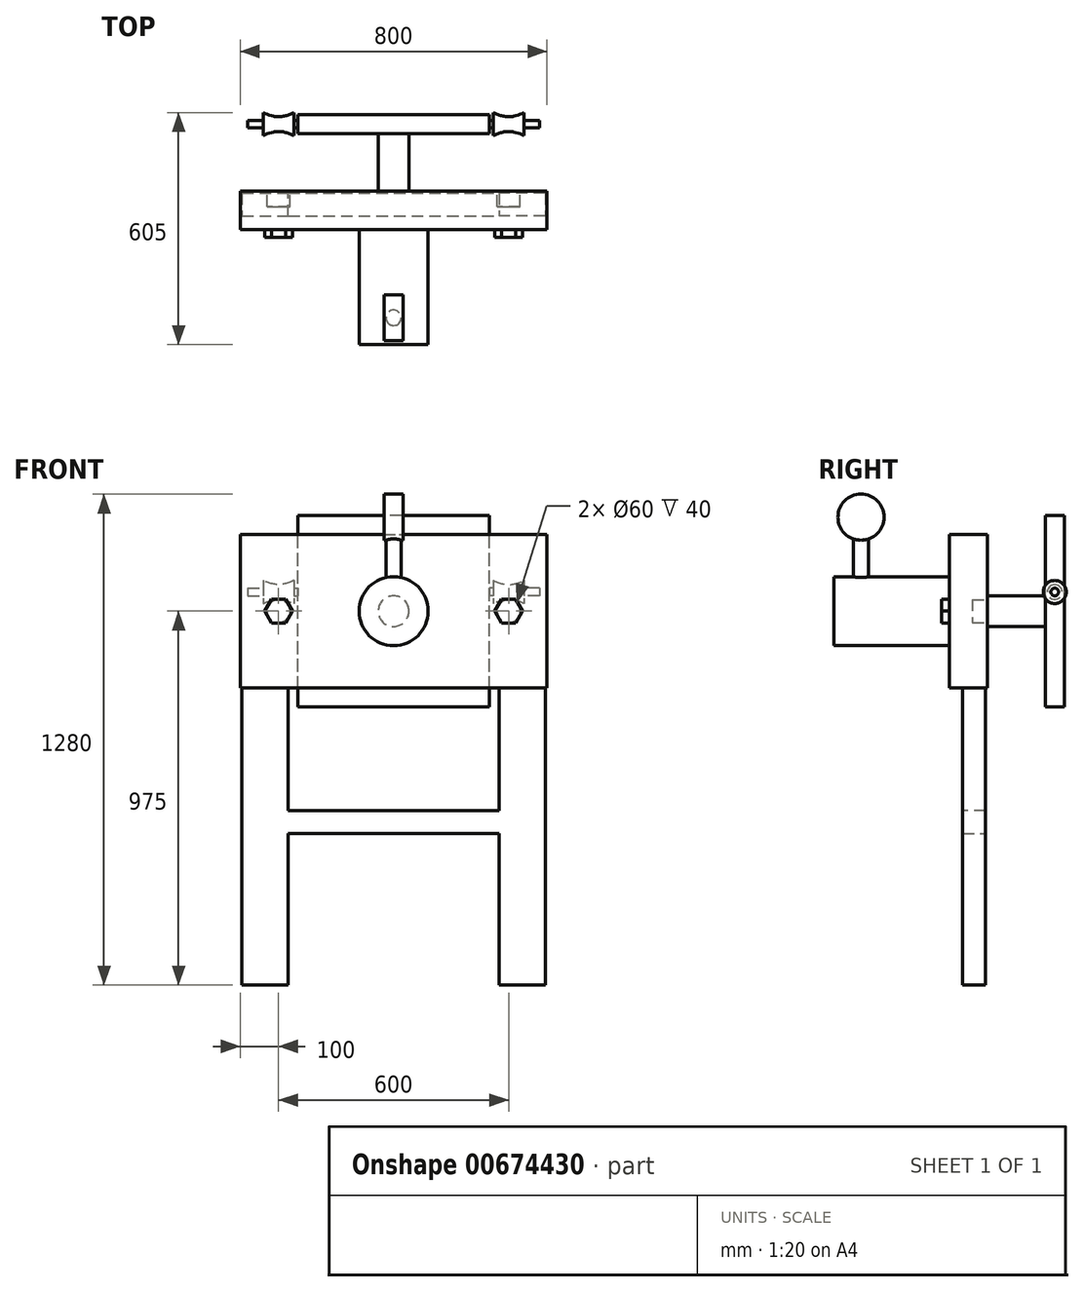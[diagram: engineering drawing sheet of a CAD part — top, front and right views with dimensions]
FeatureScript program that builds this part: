
annotation { "Feature Type Name" : "Feature", "Feature Type Description" : "" }
export const myFeature = defineFeature(function(context is Context, id is Id, definition is map)
    precondition{}
    {
        {
            var Q0;
            Q0=qCreatedBy(makeId("Front.planeOp"),FACE);
            var sketch = newSketch(context, id + "F0", { "sketchPlane" : qUnion([Q0])});
            skLineSegment(sketch, "E0.bottom", {"start": v(-400, -200) * mm, "end": v(400, -200) * mm});
            skLineSegment(sketch, "E0.top", {"start": v(-400, 200) * mm, "end": v(400, 200) * mm});
            skLineSegment(sketch, "E0.left", {"start": v(-400, -200) * mm, "end": v(-400, 200) * mm});
            skLineSegment(sketch, "E0.right", {"start": v(400, -200) * mm, "end": v(400, 200) * mm});
            skPoint(sketch, "E0.middle", {"position": v(0, 0) * mm});
            skSolve(sketch);
        }
        {
            var Q0;
            Q0=makeQuery(id+"F0.imprint","IMPRINT",FACE,{"disambiguationData":[TD([[makeQuery(id+"F0.imprint","IMPRINT",EDGE,{"derivedFrom":sQuery(id+"F0.wireOp",EDGE,"E0.bottom")}),1.0]])]});
            extrude(context, id + "F1", {"entities" : qUnion([Q0]), "endBound" : BoundingType.SYMMETRIC, "depth" : 100 * mm, "offsetDistance" : 25 * mm});
        }
        {
            var Q0;
            Q0=makeQuery(id+"F1.opExtrude","CAP_FACE",FACE,{"disambiguationData":[OSD([sQuery(id+"F0.wireOp",EDGE,"E0.bottom"),sQuery(id+"F0.wireOp",EDGE,"E0.top"),sQuery(id+"F0.wireOp",EDGE,"E0.left"),sQuery(id+"F0.wireOp",EDGE,"E0.right")])],"isStart":false});
            var sketch = newSketch(context, id + "F2", { "sketchPlane" : qUnion([Q0])});
            skCircle(sketch, "E1", {"center": v(0, 0) * mm, "radius": 90 * mm});
            skSolve(sketch);
        }
        {
            var Q0;
            Q0=makeQuery(id+"F2.imprint","IMPRINT",FACE,{"disambiguationData":[TD([[makeQuery(id+"F2.imprint","IMPRINT",EDGE,{"derivedFrom":sQuery(id+"F2.wireOp",EDGE,"E1")}),1.0]])]});
            var Q1;
            Q1=sQuery(id+"F2.wireOp",EDGE,"E1");
            extrude(context, id + "F3", {"entities" : qUnion([Q0]), "operationType" : NewBodyOperationType.ADD, "surfaceEntities" : qUnion([Q1]), "depth" : 300 * mm, "offsetDistance" : 25 * mm});
        }
        {
            var Q0;
            Q0=qCreatedBy(makeId("Top.planeOp"),FACE);
            var sketch = newSketch(context, id + "F4", { "sketchPlane" : qUnion([Q0])});
            skCircle(sketch, "E2", {"center": v(0, -280) * mm, "radius": 20 * mm});
            skSolve(sketch);
        }
        {
            var Q0;
            Q0 = qSketchRegion(id + "F4", true);
            extrude(context, id + "F5", {"entities" : qUnion([Q0]), "operationType" : NewBodyOperationType.ADD, "depth" : 200 * mm, "offsetDistance" : 25 * mm});
        }
        {
            var Q0;
            Q0=qCreatedBy(makeId("Right.planeOp"),FACE);
            var sketch = newSketch(context, id + "F6", { "sketchPlane" : qUnion([Q0])});
            skCircle(sketch, "E3", {"center": v(-280, 245) * mm, "radius": 60 * mm});
            skSolve(sketch);
        }
        {
            var Q0;
            Q0=makeQuery(id+"F6.imprint","IMPRINT",FACE,{"disambiguationData":[TD([[makeQuery(id+"F6.imprint","IMPRINT",EDGE,{"derivedFrom":sQuery(id+"F6.wireOp",EDGE,"E3")}),1.0]])]});
            extrude(context, id + "F7", {"entities" : qUnion([Q0]), "operationType" : NewBodyOperationType.ADD, "endBound" : BoundingType.SYMMETRIC, "depth" : 50 * mm, "offsetDistance" : 25 * mm});
        }
        {
            var Q0;
            Q0=makeQuery(id+"F1.opExtrude","CAP_FACE",FACE,{"disambiguationData":[OSD([sQuery(id+"F0.wireOp",EDGE,"E0.bottom"),sQuery(id+"F0.wireOp",EDGE,"E0.top"),sQuery(id+"F0.wireOp",EDGE,"E0.left"),sQuery(id+"F0.wireOp",EDGE,"E0.right")])],"isStart":false});
            var sketch = newSketch(context, id + "F8", { "sketchPlane" : qUnion([Q0])});
            skCircle(sketch, "E4.cCircle", {"center": v(-300, 0) * mm, "radius": 31.63 * mm, "construction": true});
            skLineSegment(sketch, "E4.0", {"start": v(-281.74, -31.63) * mm, "end": v(-318.26, -31.63) * mm});
            skLineSegment(sketch, "E4.1", {"start": v(-318.26, -31.63) * mm, "end": v(-336.52, 0) * mm});
            skLineSegment(sketch, "E4.2", {"start": v(-336.52, 0) * mm, "end": v(-318.26, 31.63) * mm});
            skLineSegment(sketch, "E4.3", {"start": v(-318.26, 31.63) * mm, "end": v(-281.74, 31.63) * mm});
            skLineSegment(sketch, "E4.4", {"start": v(-281.74, 31.63) * mm, "end": v(-263.48, 0) * mm});
            skLineSegment(sketch, "E4.5", {"start": v(-263.48, 0) * mm, "end": v(-281.74, -31.63) * mm});
            skPoint(sketch, "E4.0.midPoint", {"position": v(-300, -31.63) * mm});
            skLineSegment(sketch, "E5.MirrorCS", {"start": v(263.48, 0) * mm, "end": v(281.74, -31.63) * mm});
            skLineSegment(sketch, "E6.MirrorCS", {"start": v(281.74, 31.63) * mm, "end": v(263.48, 0) * mm});
            skLineSegment(sketch, "E7.MirrorCS", {"start": v(318.26, 31.63) * mm, "end": v(281.74, 31.63) * mm});
            skLineSegment(sketch, "E8.MirrorCS", {"start": v(336.52, 0) * mm, "end": v(318.26, 31.63) * mm});
            skLineSegment(sketch, "E9.MirrorCS", {"start": v(281.74, -31.63) * mm, "end": v(318.26, -31.63) * mm});
            skLineSegment(sketch, "E10.MirrorCS", {"start": v(318.26, -31.63) * mm, "end": v(336.52, 0) * mm});
            skCircle(sketch, "E11.MirrorC", {"center": v(300, 0) * mm, "radius": 31.63 * mm, "construction": true});
            skPoint(sketch, "E12.MirrorP", {"position": v(300, -31.63) * mm});
            skSolve(sketch);
        }
        {
            var Q0;
            Q0 = qSketchRegion(id + "F8", true);
            extrude(context, id + "F9", {"entities" : qUnion([Q0]), "operationType" : NewBodyOperationType.ADD, "depth" : 20 * mm, "offsetDistance" : 25 * mm});
        }
        {
            var Q0;
            Q0=makeQuery(id+"F1.opExtrude","CAP_FACE",FACE,{"disambiguationData":[OSD([sQuery(id+"F0.wireOp",EDGE,"E0.bottom"),sQuery(id+"F0.wireOp",EDGE,"E0.top"),sQuery(id+"F0.wireOp",EDGE,"E0.left"),sQuery(id+"F0.wireOp",EDGE,"E0.right")])],"isStart":true});
            var sketch = newSketch(context, id + "F10", { "sketchPlane" : qUnion([Q0])});
            skCircle(sketch, "E13", {"center": v(-300, 0) * mm, "radius": 30 * mm});
            skCircle(sketch, "E14", {"center": v(300, 0) * mm, "radius": 30 * mm});
            skSolve(sketch);
        }
        {
            var Q0;
            Q0 = qSketchRegion(id + "F10", true);
            extrude(context, id + "F11", {"entities" : qUnion([Q0]), "operationType" : NewBodyOperationType.REMOVE, "oppositeDirection" : true, "depth" : 40 * mm, "offsetDistance" : 25 * mm});
        }
        {
            var Q0;
            Q0=makeQuery(id+"F1.opExtrude","SWEPT_FACE",FACE,{"disambiguationData":[OSD([sQuery(id+"F0.wireOp",EDGE,"E0.bottom")])]});
            var sketch = newSketch(context, id + "F12", { "sketchPlane" : qUnion([Q0])});
            skLineSegment(sketch, "E15.bottom", {"start": v(395, -45) * mm, "end": v(275, -45) * mm});
            skLineSegment(sketch, "E15.top", {"start": v(395, 15) * mm, "end": v(275, 15) * mm});
            skLineSegment(sketch, "E15.left", {"start": v(395, -45) * mm, "end": v(395, 15) * mm});
            skLineSegment(sketch, "E15.right", {"start": v(275, -45) * mm, "end": v(275, 15) * mm});
            skLineSegment(sketch, "E16.MirrorCS", {"start": v(-275, -45) * mm, "end": v(-275, 15) * mm});
            skLineSegment(sketch, "E17.MirrorCS", {"start": v(-395, -45) * mm, "end": v(-395, 15) * mm});
            skLineSegment(sketch, "E18.MirrorCS", {"start": v(-395, -45) * mm, "end": v(-275, -45) * mm});
            skLineSegment(sketch, "E19.MirrorCS", {"start": v(-395, 15) * mm, "end": v(-275, 15) * mm});
            skSolve(sketch);
        }
        {
            var Q0;
            Q0 = qSketchRegion(id + "F12", true);
            extrude(context, id + "F13", {"entities" : qUnion([Q0]), "operationType" : NewBodyOperationType.ADD, "depth" : 775 * mm, "offsetDistance" : 25 * mm});
        }
        {
            var Q0;
            Q0=makeQuery(id+"F1.opExtrude","CAP_FACE",FACE,{"disambiguationData":[OSD([sQuery(id+"F0.wireOp",EDGE,"E0.bottom"),sQuery(id+"F0.wireOp",EDGE,"E0.top"),sQuery(id+"F0.wireOp",EDGE,"E0.left"),sQuery(id+"F0.wireOp",EDGE,"E0.right")])],"isStart":true});
            var sketch = newSketch(context, id + "F14", { "sketchPlane" : qUnion([Q0])});
            skCircle(sketch, "E20", {"center": v(0, 0) * mm, "radius": 40 * mm});
            skSolve(sketch);
        }
        {
            var Q0;
            Q0=makeQuery(id+"F14.imprint","IMPRINT",FACE,{"disambiguationData":[TD([[makeQuery(id+"F14.imprint","IMPRINT",EDGE,{"derivedFrom":sQuery(id+"F14.wireOp",EDGE,"E20")}),1.0]])]});
            var Q1;
            Q1=sQuery(id+"F14.wireOp",EDGE,"E20");
            extrude(context, id + "F15", {"entities" : qUnion([Q0]), "operationType" : NewBodyOperationType.ADD, "surfaceEntities" : qUnion([Q1]), "depth" : 150 * mm, "offsetDistance" : 25 * mm});
        }
        {
            var Q0;
            Q0=makeQuery(id+"F15.opExtrude","CAP_FACE",FACE,{"disambiguationData":[OSD([sQuery(id+"F14.wireOp",EDGE,"E20")])],"isStart":false});
            var sketch = newSketch(context, id + "F16", { "sketchPlane" : qUnion([Q0])});
            skLineSegment(sketch, "E21.bottom", {"start": v(-250, -250) * mm, "end": v(250, -250) * mm});
            skLineSegment(sketch, "E21.top", {"start": v(-250, 250) * mm, "end": v(250, 250) * mm});
            skLineSegment(sketch, "E21.left", {"start": v(-250, -250) * mm, "end": v(-250, 250) * mm});
            skLineSegment(sketch, "E21.right", {"start": v(250, -250) * mm, "end": v(250, 250) * mm});
            skPoint(sketch, "E21.middle", {"position": v(0, 0) * mm});
            skSolve(sketch);
        }
        {
            var Q0;
            Q0 = qSketchRegion(id + "F16", true);
            extrude(context, id + "F17", {"entities" : qUnion([Q0]), "operationType" : NewBodyOperationType.ADD, "depth" : 50 * mm, "offsetDistance" : 25 * mm});
        }
        {
            var Q0;
            Q0=makeQuery(id+"F17.opExtrude","SWEPT_FACE",FACE,{"disambiguationData":[OSD([sQuery(id+"F16.wireOp",EDGE,"E21.right")])]});
            var sketch = newSketch(context, id + "F18", { "sketchPlane" : qUnion([Q0])});
            skCircle(sketch, "E22", {"center": v(-225, 50) * mm, "radius": 10 * mm});
            skSolve(sketch);
        }
        {
            var Q0;
            Q0=makeQuery(id+"F18.imprint","IMPRINT",FACE,{"disambiguationData":[TD([[makeQuery(id+"F18.imprint","IMPRINT",EDGE,{"derivedFrom":sQuery(id+"F18.wireOp",EDGE,"E22")}),1.0]])]});
            extrude(context, id + "F19", {"entities" : qUnion([Q0]), "operationType" : NewBodyOperationType.ADD, "depth" : 130 * mm, "offsetDistance" : 25 * mm});
        }
        {
            var Q0;
            Q0=makeQuery(id+"F17.opExtrude","CAP_FACE",FACE,{"disambiguationData":[OSD([sQuery(id+"F16.wireOp",EDGE,"E21.bottom"),sQuery(id+"F16.wireOp",EDGE,"E21.top"),sQuery(id+"F16.wireOp",EDGE,"E21.left"),sQuery(id+"F16.wireOp",EDGE,"E21.right")])],"isStart":false});
            cPlane(context, id + "F20", {"entities" : qUnion([Q0]), "cplaneType" : CPlaneType.OFFSET, "offset" : 25 * mm, "oppositeDirection" : true, "width" : 150 * mm, "height" : 150 * mm});
        }
        {
            var Q0;
            Q0=makeQuery(id+"F17.opExtrude","SWEPT_FACE",FACE,{"disambiguationData":[OSD([sQuery(id+"F16.wireOp",EDGE,"E21.top")])]});
            cPlane(context, id + "F21", {"entities" : qUnion([Q0]), "cplaneType" : CPlaneType.OFFSET, "offset" : 200 * mm, "oppositeDirection" : true, "width" : 150 * mm, "height" : 150 * mm});
        }
        {
            var Q0;
            Q0=qCreatedBy(id+"F20.planeOp",FACE);
            var sketch = newSketch(context, id + "F22", { "sketchPlane" : qUnion([Q0])});
            skLineSegment(sketch, "E23.bottom", {"start": v(260, 40) * mm, "end": v(340, 40) * mm});
            skLineSegment(sketch, "E23.left", {"start": v(260, 40) * mm, "end": v(260, 20) * mm});
            skLineSegment(sketch, "E23.right", {"start": v(340, 40) * mm, "end": v(340, 20) * mm});
            skFitSpline(sketch, "E24", {"points": [v(260, 20) * mm, v(300.1, 30.83) * mm, v(340, 20) * mm], "startDerivative": vector(79.63, 37.47) * mm, "endDerivative": vector(80.36, -37.4) * mm});
            skSolve(sketch);
        }
        {
            var Q0;
            Q0=makeQuery(id+"F22.imprint","IMPRINT",FACE,{"disambiguationData":[TD([[makeQuery(id+"F22.imprint","IMPRINT",EDGE,{"derivedFrom":sQuery(id+"F22.wireOp",EDGE,"E23.bottom")}),-1.0]])]});
            var Q1;
            Q1=makeQuery(id+"F19.opExtrude","SWEPT_FACE",FACE,{"disambiguationData":[OSD([sQuery(id+"F18.wireOp",EDGE,"E22")])]});
            revolve(context, id + "F23", {"operationType" : NewBodyOperationType.ADD, "entities" : qUnion([Q0]), "axis" : qUnion([Q1]), "revolveType" : RevolveType.FULL});
        }
        {
            var Q0;
            Q0=makeQuery(id+"F1.opExtrude","SWEPT_BODY",BODY,{"disambiguationData":[OSD([sQuery(id+"F0.wireOp",EDGE,"E0.bottom"),sQuery(id+"F0.wireOp",EDGE,"E0.top"),sQuery(id+"F0.wireOp",EDGE,"E0.left"),sQuery(id+"F0.wireOp",EDGE,"E0.right")])]});
            var Q1;
            Q1=qCreatedBy(makeId("Right.planeOp"),FACE);
            mirror(context, id + "F24", {"operationType" : NewBodyOperationType.ADD, "entities" : qUnion([Q0]), "mirrorPlane" : qUnion([Q1])});
        }
        {
            var Q0;
            Q0=makeQuery(id+"F13.opExtrude","SWEPT_FACE",FACE,{"disambiguationData":[OSD([sQuery(id+"F12.wireOp",EDGE,"E15.right")])]});
            var sketch = newSketch(context, id + "F25", { "sketchPlane" : qUnion([Q0])});
            skLineSegment(sketch, "E25.bottom", {"start": v(-45, -520) * mm, "end": v(15, -520) * mm});
            skLineSegment(sketch, "E25.top", {"start": v(-45, -580) * mm, "end": v(15, -580) * mm});
            skLineSegment(sketch, "E25.left", {"start": v(-45, -520) * mm, "end": v(-45, -580) * mm});
            skLineSegment(sketch, "E25.right", {"start": v(15, -520) * mm, "end": v(15, -580) * mm});
            skSolve(sketch);
        }
        {
            var Q0;
            Q0=makeQuery(id+"F25.imprint","IMPRINT",FACE,{"disambiguationData":[TD([[makeQuery(id+"F25.imprint","IMPRINT",EDGE,{"derivedFrom":sQuery(id+"F25.wireOp",EDGE,"E25.bottom")}),-1.0]])]});
            extrude(context, id + "F26", {"entities" : qUnion([Q0]), "operationType" : NewBodyOperationType.ADD, "depth" : 600 * mm, "offsetDistance" : 25 * mm});
        }
    });
